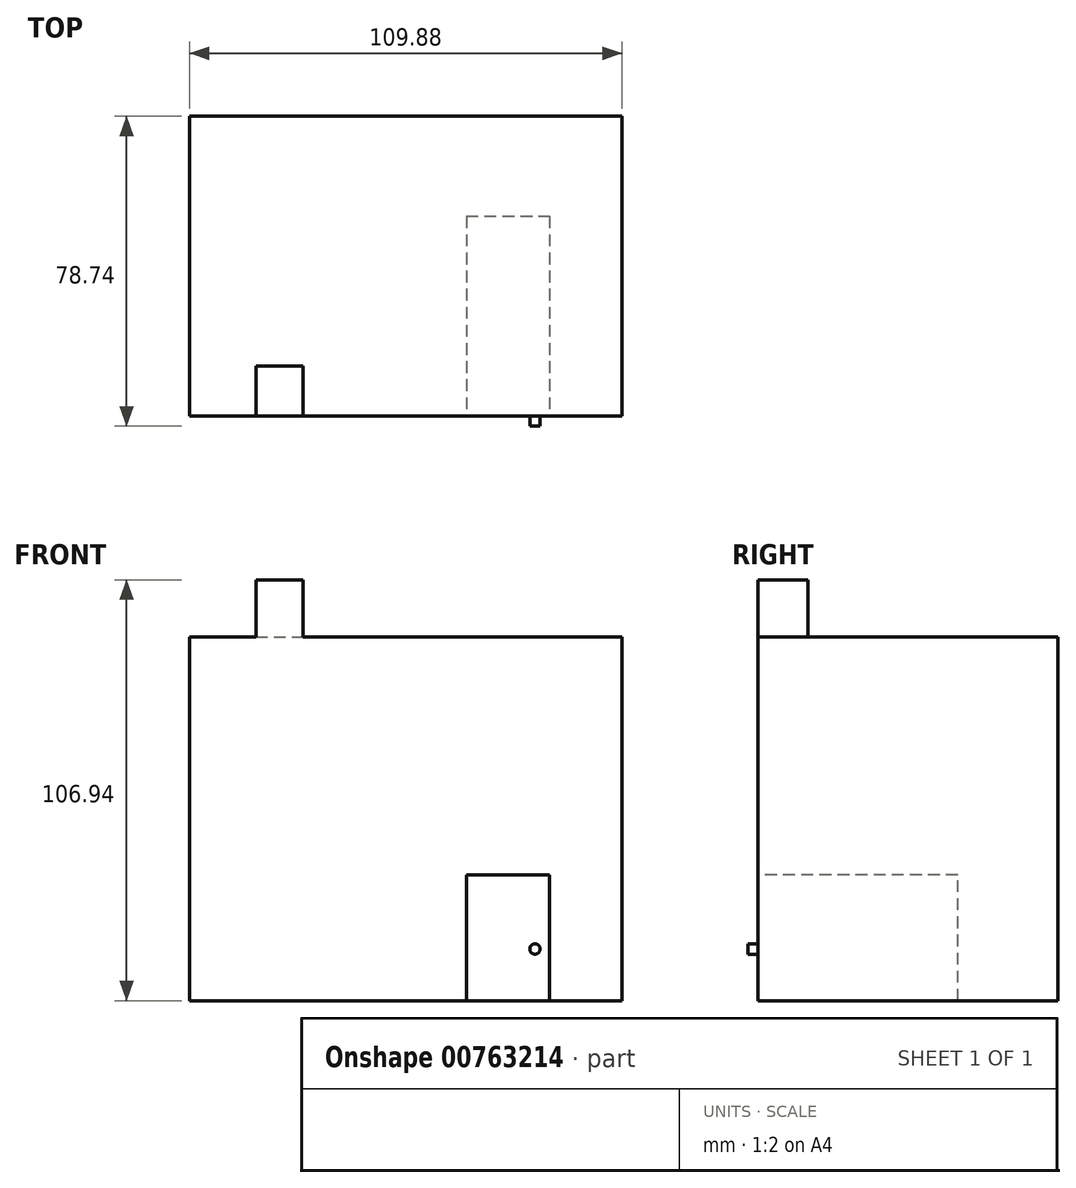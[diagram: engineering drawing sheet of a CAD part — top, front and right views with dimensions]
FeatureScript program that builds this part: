
annotation { "Feature Type Name" : "Feature", "Feature Type Description" : "" }
export const myFeature = defineFeature(function(context is Context, id is Id, definition is map)
    precondition{}
    {
        {
            var Q0;
            Q0=qCreatedBy(makeId("Front.planeOp"),FACE);
            var sketch = newSketch(context, id + "F0", { "sketchPlane" : qUnion([Q0])});
            skLineSegment(sketch, "E0.bottom", {"start": v(-40.45, -49.75) * mm, "end": v(69.43, -49.75) * mm});
            skLineSegment(sketch, "E0.top", {"start": v(-40.45, 42.7) * mm, "end": v(69.43, 42.7) * mm});
            skLineSegment(sketch, "E0.left", {"start": v(-40.45, -49.75) * mm, "end": v(-40.45, 42.7) * mm});
            skLineSegment(sketch, "E0.right", {"start": v(69.43, -49.75) * mm, "end": v(69.43, 42.7) * mm});
            skLineSegment(sketch, "E1", {"start": v(29.87, -49.75) * mm, "end": v(29.87, -74.04) * mm});
            skLineSegment(sketch, "E2", {"start": v(29.87, -74.04) * mm, "end": v(51.02, -74.04) * mm});
            skLineSegment(sketch, "E3", {"start": v(51.02, -74.04) * mm, "end": v(51.02, -62.48) * mm});
            skLineSegment(sketch, "E4", {"start": v(51.02, -62.48) * mm, "end": v(29.87, -62.48) * mm});
            skLineSegment(sketch, "E5", {"start": v(29.87, -62.48) * mm, "end": v(29.87, -49.75) * mm});
            skLineSegment(sketch, "E6", {"start": v(51.02, -49.75) * mm, "end": v(51.02, -62.48) * mm});
            skLineSegment(sketch, "E7", {"start": v(29.87, -49.75) * mm, "end": v(29.87, -17.82) * mm});
            skLineSegment(sketch, "E8", {"start": v(29.87, -17.82) * mm, "end": v(51.02, -17.82) * mm});
            skLineSegment(sketch, "E9", {"start": v(51.02, -17.82) * mm, "end": v(51.02, -49.75) * mm});
            skLineSegment(sketch, "E10", {"start": v(-23.6, 42.7) * mm, "end": v(-23.6, 57.2) * mm});
            skLineSegment(sketch, "E11", {"start": v(-23.6, 57.2) * mm, "end": v(-11.65, 57.2) * mm});
            skLineSegment(sketch, "E12", {"start": v(-11.65, 57.2) * mm, "end": v(-11.65, 42.7) * mm});
            skSolve(sketch);
        }
        {
            var Q0;
            {var subQ3=sQuery(id+"F0.wireOp",EDGE,"E0.left");Q0=makeQuery(id+"F0.imprint","IMPRINT",FACE,{"disambiguationData":[TD([[makeQuery(id+"F0.imprint","IMPRINT",EDGE,{"derivedFrom":subQ3}),-1.0]])]});}
            extrude(context, id + "F1", {"entities" : qUnion([Q0]), "depth" : -76.2 * mm, "offsetDistance" : 25.4 * mm});
        }
        {
            var Q0;
            {var subQ0=sQuery(id+"F0.wireOp",EDGE,"E10");Q0=makeQuery(id+"F0.imprint","IMPRINT",FACE,{"disambiguationData":[TD([[makeQuery(id+"F0.imprint","IMPRINT",EDGE,{"derivedFrom":subQ0}),-1.0]])]});}
            extrude(context, id + "F2", {"entities" : qUnion([Q0]), "operationType" : NewBodyOperationType.ADD, "depth" : -12.7 * mm, "offsetDistance" : 25.4 * mm});
        }
        {
            var Q0;
            {var subQ0=sQuery(id+"F0.wireOp",EDGE,"E7");Q0=makeQuery(id+"F0.imprint","IMPRINT",FACE,{"disambiguationData":[TD([[makeQuery(id+"F0.imprint","IMPRINT",EDGE,{"derivedFrom":subQ0}),-1.0]])]});}
            var sketch = newSketch(context, id + "F3", { "sketchPlane" : qUnion([Q0])});
            skCircle(sketch, "E13", {"center": v(47.3, -36.63) * mm, "radius": 1.31 * mm});
            skSolve(sketch);
        }
        {
            var Q0;
            Q0=makeQuery(id+"F3.imprint","IMPRINT",FACE,{"disambiguationData":[TD([[makeQuery(id+"F3.imprint","IMPRINT",EDGE,{"derivedFrom":sQuery(id+"F3.wireOp",EDGE,"E13")}),1.0]])]});
            extrude(context, id + "F4", {"entities" : qUnion([Q0]), "depth" : 2.54 * mm, "offsetDistance" : 25.4 * mm});
        }
        {
            var Q0;
            Q0=makeQuery(id+"F1.opExtrude","CAP_FACE",FACE,{"disambiguationData":[OSD([sQuery(id+"F0.wireOp",EDGE,"E0.bottom"),sQuery(id+"F0.wireOp",EDGE,"E0.top"),sQuery(id+"F0.wireOp",EDGE,"E0.left"),sQuery(id+"F0.wireOp",EDGE,"E0.right"),sQuery(id+"F0.wireOp",EDGE,"E7"),sQuery(id+"F0.wireOp",EDGE,"E8"),sQuery(id+"F0.wireOp",EDGE,"E9")])],"isStart":false});
            var sketch = newSketch(context, id + "F5", { "sketchPlane" : qUnion([Q0])});
            skLineSegment(sketch, "E14.bottom", {"start": v(-51.02, -17.82) * mm, "end": v(-29.87, -17.82) * mm});
            skLineSegment(sketch, "E14.top", {"start": v(-51.02, -49.75) * mm, "end": v(-29.87, -49.75) * mm});
            skLineSegment(sketch, "E14.left", {"start": v(-51.02, -17.82) * mm, "end": v(-51.02, -49.75) * mm});
            skLineSegment(sketch, "E14.right", {"start": v(-29.87, -17.82) * mm, "end": v(-29.87, -49.75) * mm});
            skSolve(sketch);
        }
        {
            var Q0;
            Q0=makeQuery(id+"F5.imprint","IMPRINT",FACE,{"disambiguationData":[TD([[makeQuery(id+"F5.imprint","IMPRINT",EDGE,{"derivedFrom":sQuery(id+"F5.wireOp",EDGE,"E14.bottom")}),1.0]])]});
            extrude(context, id + "F6", {"entities" : qUnion([Q0]), "operationType" : NewBodyOperationType.ADD, "depth" : -25.4 * mm, "offsetDistance" : 25.4 * mm});
        }
    });
